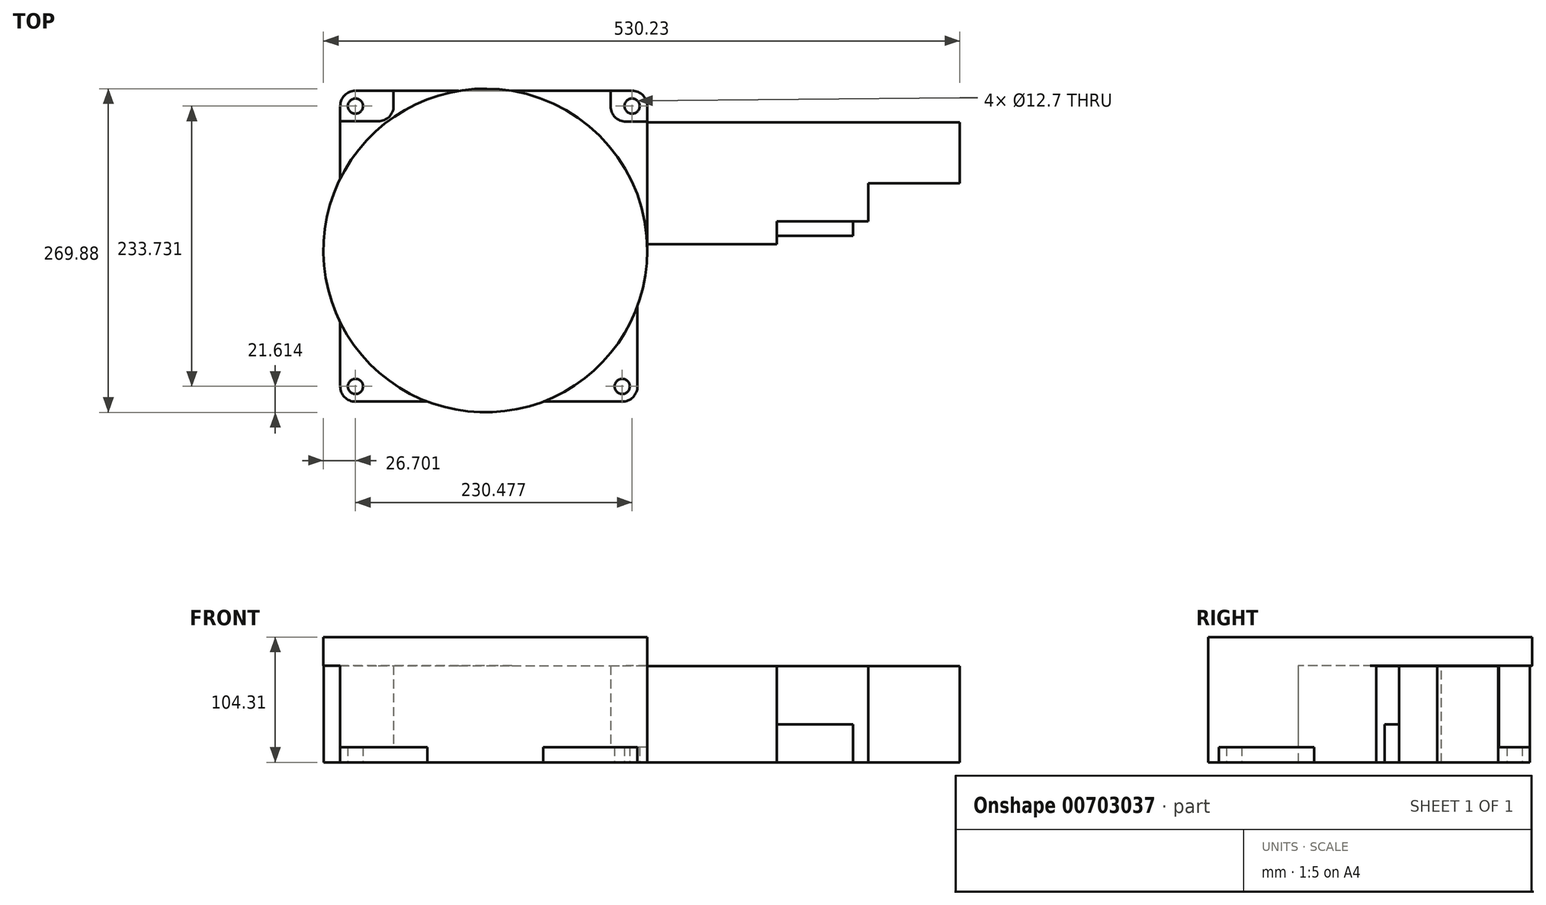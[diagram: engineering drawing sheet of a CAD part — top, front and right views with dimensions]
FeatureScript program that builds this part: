
annotation { "Feature Type Name" : "Feature", "Feature Type Description" : "" }
export const myFeature = defineFeature(function(context is Context, id is Id, definition is map)
    precondition{}
    {
        {
            var Q0;
            Q0=qCreatedBy(makeId("Top.planeOp"),FACE);
            var sketch = newSketch(context, id + "F0", { "sketchPlane" : qUnion([Q0])});
            skLineSegment(sketch, "E0.bottom", {"start": v(-108.24, 133.1) * mm, "end": v(122.24, 133.1) * mm});
            skLineSegment(sketch, "E0.top", {"start": v(-108.24, -126.03) * mm, "end": v(-48.23, -126.03) * mm});
            skLineSegment(sketch, "E0.left", {"start": v(-120.94, 120.4) * mm, "end": v(-120.94, 59.45) * mm});
            skLineSegment(sketch, "E0.right", {"start": v(134.94, 120.4) * mm, "end": v(134.94, 0) * mm});
            skLineSegment(sketch, "E1", {"start": v(126.71, -46.38) * mm, "end": v(126.71, -46.4) * mm});
            skArc(sketch, "E2.filletArc", {"start": v(114.01, -126.03) * mm, "mid": v(123, -122.3) * mm, "end": v(126.71, -113.33) * mm});
            skPoint(sketch, "E3.visualSharp", {"position": v(134.94, 133.1) * mm});
            skArc(sketch, "E3.filletArc", {"start": v(134.94, 120.4) * mm, "mid": v(131.22, 129.39) * mm, "end": v(122.24, 133.1) * mm});
            skPoint(sketch, "E4.visualSharp", {"position": v(-120.94, 133.1) * mm});
            skArc(sketch, "E4.filletArc", {"start": v(-108.24, 133.1) * mm, "mid": v(-117.22, 129.39) * mm, "end": v(-120.94, 120.4) * mm});
            skPoint(sketch, "E5.visualSharp", {"position": v(-120.94, -126.03) * mm});
            skArc(sketch, "E5.filletArc", {"start": v(-120.94, -113.33) * mm, "mid": v(-117.22, -122.3) * mm, "end": v(-108.24, -126.03) * mm});
            skArc(sketch, "E6", {"start": v(-48.23, -126.03) * mm, "mid": v(0, -134.94) * mm, "end": v(48.23, -126.03) * mm});
            skLineSegment(sketch, "E7", {"start": v(126.71, -46.38) * mm, "end": v(126.71, -113.33) * mm});
            skArc(sketch, "E8", {"start": v(126.71, -46.4) * mm, "mid": v(132.86, -23.56) * mm, "end": v(134.94, 0) * mm});
            skLineSegment(sketch, "E9", {"start": v(48.23, -126.03) * mm, "end": v(114.01, -126.03) * mm});
            skArc(sketch, "E10", {"start": v(-120.94, 59.45) * mm, "mid": v(-134.76, 0) * mm, "end": v(-120.94, -59.45) * mm});
            skLineSegment(sketch, "E11", {"start": v(-120.94, -59.45) * mm, "end": v(-120.94, -113.33) * mm});
            skSolve(sketch);
        }
        {
            var Q0;
            Q0 = qSketchRegion(id + "F0", true);
            extrude(context, id + "F1", {"entities" : qUnion([Q0]), "oppositeDirection" : true, "depth" : 12.7 * mm, "offsetDistance" : 25.4 * mm});
        }
        {
            var Q0;
            Q0=makeQuery(id+"F1.opExtrude","CAP_FACE",FACE,{"disambiguationData":[OSD([sQuery(id+"F0.wireOp",EDGE,"E0.bottom"),sQuery(id+"F0.wireOp",EDGE,"E0.top"),sQuery(id+"F0.wireOp",EDGE,"E0.left"),sQuery(id+"F0.wireOp",EDGE,"E0.right"),sQuery(id+"F0.wireOp",EDGE,"E2.filletArc"),sQuery(id+"F0.wireOp",EDGE,"E3.filletArc"),sQuery(id+"F0.wireOp",EDGE,"E4.filletArc"),sQuery(id+"F0.wireOp",EDGE,"E5.filletArc"),sQuery(id+"F0.wireOp",EDGE,"E6"),sQuery(id+"F0.wireOp",EDGE,"E7"),sQuery(id+"F0.wireOp",EDGE,"E8"),sQuery(id+"F0.wireOp",EDGE,"E9")])],"isStart":false});
            var sketch = newSketch(context, id + "F2", { "sketchPlane" : qUnion([Q0])});
            skCircle(sketch, "E12", {"center": v(-108.24, -120.4) * mm, "radius": 6.35 * mm});
            skCircle(sketch, "E13", {"center": v(122.24, -120.4) * mm, "radius": 6.35 * mm});
            skCircle(sketch, "E14", {"center": v(-108.24, 113.33) * mm, "radius": 6.35 * mm});
            skCircle(sketch, "E15", {"center": v(114.01, 113.33) * mm, "radius": 6.35 * mm});
            skSolve(sketch);
        }
        {
            var Q0;
            Q0 = qSketchRegion(id + "F2", true);
            var Q1;
            Q1=makeQuery(id+"F1.opExtrude","CAP_FACE",FACE,{"disambiguationData":[OSD([sQuery(id+"F0.wireOp",EDGE,"E0.bottom"),sQuery(id+"F0.wireOp",EDGE,"E0.top"),sQuery(id+"F0.wireOp",EDGE,"E0.left"),sQuery(id+"F0.wireOp",EDGE,"E0.right"),sQuery(id+"F0.wireOp",EDGE,"E2.filletArc"),sQuery(id+"F0.wireOp",EDGE,"E3.filletArc"),sQuery(id+"F0.wireOp",EDGE,"E4.filletArc"),sQuery(id+"F0.wireOp",EDGE,"E5.filletArc"),sQuery(id+"F0.wireOp",EDGE,"E6"),sQuery(id+"F0.wireOp",EDGE,"E7"),sQuery(id+"F0.wireOp",EDGE,"E8"),sQuery(id+"F0.wireOp",EDGE,"E9")])],"isStart":true});
            var Q2;
            Q2=sQuery(id+"F2.wireOp",EDGE,"E13");
            var Q3;
            Q3=sQuery(id+"F2.wireOp",EDGE,"E12");
            var Q4;
            Q4=sQuery(id+"F2.wireOp",EDGE,"E14");
            var Q5;
            Q5=sQuery(id+"F2.wireOp",EDGE,"E15");
            extrude(context, id + "F3", {"entities" : qUnion([Q0, Q1]), "operationType" : NewBodyOperationType.REMOVE, "surfaceEntities" : qUnion([Q2, Q3, Q4, Q5]), "endBound" : BoundingType.THROUGH_ALL, "oppositeDirection" : true, "depth" : -12.7 * mm, "offsetDistance" : 25.4 * mm});
        }
        {
            var Q0;
            Q0=makeQuery(id+"F1.opExtrude","CAP_FACE",FACE,{"disambiguationData":[OSD([sQuery(id+"F0.wireOp",EDGE,"E0.bottom"),sQuery(id+"F0.wireOp",EDGE,"E0.top"),sQuery(id+"F0.wireOp",EDGE,"E0.left"),sQuery(id+"F0.wireOp",EDGE,"E0.right"),sQuery(id+"F0.wireOp",EDGE,"E2.filletArc"),sQuery(id+"F0.wireOp",EDGE,"E3.filletArc"),sQuery(id+"F0.wireOp",EDGE,"E4.filletArc"),sQuery(id+"F0.wireOp",EDGE,"E5.filletArc"),sQuery(id+"F0.wireOp",EDGE,"E6"),sQuery(id+"F0.wireOp",EDGE,"E7"),sQuery(id+"F0.wireOp",EDGE,"E8"),sQuery(id+"F0.wireOp",EDGE,"E9")])],"isStart":true});
            var sketch = newSketch(context, id + "F4", { "sketchPlane" : qUnion([Q0])});
            skLineSegment(sketch, "E16", {"start": v(-76.49, 133.1) * mm, "end": v(-76.49, 120.4) * mm});
            skLineSegment(sketch, "E17", {"start": v(-120.94, 107.7) * mm, "end": v(-89.19, 107.7) * mm});
            skLineSegment(sketch, "E18", {"start": v(104.3, 133.1) * mm, "end": v(104.3, 120.11) * mm});
            skLineSegment(sketch, "E19", {"start": v(134.94, 107.41) * mm, "end": v(117, 107.41) * mm});
            skArc(sketch, "E20.filletArc", {"start": v(-89.19, 107.7) * mm, "mid": v(-80.2, 111.43) * mm, "end": v(-76.49, 120.4) * mm});
            skArc(sketch, "E21.filletArc", {"start": v(104.3, 120.11) * mm, "mid": v(108.02, 111.13) * mm, "end": v(117, 107.41) * mm});
            skLineSegment(sketch, "E22", {"start": v(98.35, -126.03) * mm, "end": v(98.35, -102.17) * mm});
            skLineSegment(sketch, "E23", {"start": v(98.35, -102.17) * mm, "end": v(126.71, -102.17) * mm});
            skArc(sketch, "E24", {"start": v(-120.3, 61.13) * mm, "mid": v(-31.43, -131.23) * mm, "end": v(134.94, 0) * mm});
            skLineSegment(sketch, "E25", {"start": v(134.94, 107.41) * mm, "end": v(134.94, 0) * mm});
            skSolve(sketch);
        }
        {
            var Q0;
            {var subQ5=sQuery(id+"F4.wireOp",EDGE,"E16");Q0=makeQuery(id+"F4.imprint","IMPRINT",FACE,{"disambiguationData":[TD([[makeQuery(id+"F4.imprint","IMPRINT",EDGE,{"derivedFrom":subQ5}),1.0]])]});}
            extrude(context, id + "F5", {"entities" : qUnion([Q0]), "operationType" : NewBodyOperationType.ADD, "depth" : 67.8 * mm, "offsetDistance" : 25.4 * mm});
        }
        {
            var Q0;
            Q0=makeQuery(id+"F5.opExtrude","CAP_FACE",FACE,{"disambiguationData":[OSD([sQuery(id+"F0.wireOp",EDGE,"E0.bottom"),sQuery(id+"F0.wireOp",EDGE,"E0.left"),sQuery(id+"F0.wireOp",EDGE,"E10"),sQuery(id+"F0.wireOp",EDGE,"E11"),sQuery(id+"F4.wireOp",EDGE,"E16"),sQuery(id+"F4.wireOp",EDGE,"E17"),sQuery(id+"F4.wireOp",EDGE,"E18"),sQuery(id+"F4.wireOp",EDGE,"E19"),sQuery(id+"F4.wireOp",EDGE,"E20.filletArc"),sQuery(id+"F4.wireOp",EDGE,"E21.filletArc"),sQuery(id+"F4.wireOp",EDGE,"E24"),sQuery(id+"F4.wireOp",EDGE,"E25")])],"isStart":false});
            var sketch = newSketch(context, id + "F6", { "sketchPlane" : qUnion([Q0])});
            skCircle(sketch, "E26", {"center": v(0, 0) * mm, "radius": 134.94 * mm});
            skSolve(sketch);
        }
        {
            var Q0;
            Q0 = qSketchRegion(id + "F6", true);
            var Q1;
            Q1 = qSketchRegion(id + "F8", true);
            extrude(context, id + "F7", {"entities" : qUnion([Q0, Q1]), "operationType" : NewBodyOperationType.ADD, "depth" : 23.8 * mm, "offsetDistance" : 25.4 * mm});
        }
        {
            var Q0;
            Q0=makeQuery(id+"F7.opExtrude","CAP_FACE",FACE,{"disambiguationData":[OSD([sQuery(id+"F6.wireOp",EDGE,"E26")])],"isStart":false});
            var sketch = newSketch(context, id + "F8", { "sketchPlane" : qUnion([Q0])});
            skCircle(sketch, "E27", {"center": v(-57.15, 57.15) * mm, "radius": 5 * mm});
            skCircle(sketch, "E28", {"center": v(57.15, 57.15) * mm, "radius": 5 * mm});
            skCircle(sketch, "E29", {"center": v(57.15, -57.15) * mm, "radius": 5 * mm});
            skCircle(sketch, "E30", {"center": v(-57.15, -57.15) * mm, "radius": 5 * mm});
            skSolve(sketch);
        }
        {
            var Q0;
            Q0=makeQuery(id+"F5.boolean.opBoolean","MERGE",FACE,{"derivedFrom":[makeQuery(id+"F1.opExtrude","SWEPT_FACE",FACE,{"disambiguationData":[OSD([sQuery(id+"F0.wireOp",EDGE,"E0.right")])]}),makeQuery(id+"F5.opExtrude","SWEPT_FACE",FACE,{"disambiguationData":[OSD([sQuery(id+"F4.wireOp",EDGE,"E25")])]})]});
            var sketch = newSketch(context, id + "F9", { "sketchPlane" : qUnion([Q0])});
            skLineSegment(sketch, "E31.bottom", {"start": v(5.35, 67.38) * mm, "end": v(106.95, 67.38) * mm});
            skLineSegment(sketch, "E31.top", {"start": v(5.35, -12.7) * mm, "end": v(106.95, -12.7) * mm});
            skLineSegment(sketch, "E31.left", {"start": v(5.35, 67.38) * mm, "end": v(5.35, -12.7) * mm});
            skLineSegment(sketch, "E31.right", {"start": v(106.95, 67.38) * mm, "end": v(106.95, -12.7) * mm});
            skSolve(sketch);
        }
        {
            var Q0;
            Q0 = qSketchRegion(id + "F9", true);
            extrude(context, id + "F10", {"entities" : qUnion([Q0]), "operationType" : NewBodyOperationType.ADD, "depth" : 107.95 * mm, "offsetDistance" : 25.4 * mm});
        }
        {
            var Q0;
            Q0=makeQuery(id+"F10.opExtrude","CAP_FACE",FACE,{"disambiguationData":[OSD([sQuery(id+"F9.wireOp",EDGE,"E31.bottom"),sQuery(id+"F9.wireOp",EDGE,"E31.top"),sQuery(id+"F9.wireOp",EDGE,"E31.left"),sQuery(id+"F9.wireOp",EDGE,"E31.right")])],"isStart":false});
            var sketch = newSketch(context, id + "F11", { "sketchPlane" : qUnion([Q0])});
            skLineSegment(sketch, "E32.bottom", {"start": v(24.4, 67.38) * mm, "end": v(106.95, 67.38) * mm});
            skLineSegment(sketch, "E32.top", {"start": v(24.4, -12.7) * mm, "end": v(106.95, -12.7) * mm});
            skLineSegment(sketch, "E32.left", {"start": v(24.4, 67.38) * mm, "end": v(24.4, -12.7) * mm});
            skLineSegment(sketch, "E32.right", {"start": v(106.95, 67.38) * mm, "end": v(106.95, -12.7) * mm});
            skSolve(sketch);
        }
        {
            var Q0;
            Q0 = qSketchRegion(id + "F11", true);
            extrude(context, id + "F12", {"entities" : qUnion([Q0]), "operationType" : NewBodyOperationType.ADD, "depth" : 76.2 * mm, "offsetDistance" : 25.4 * mm});
        }
        {
            var Q0;
            Q0=makeQuery(id+"F10.opExtrude","CAP_FACE",FACE,{"disambiguationData":[OSD([sQuery(id+"F9.wireOp",EDGE,"E31.bottom"),sQuery(id+"F9.wireOp",EDGE,"E31.top"),sQuery(id+"F9.wireOp",EDGE,"E31.left"),sQuery(id+"F9.wireOp",EDGE,"E31.right")])],"isStart":false});
            var sketch = newSketch(context, id + "F13", { "sketchPlane" : qUnion([Q0])});
            skLineSegment(sketch, "E33.bottom", {"start": v(12.1, 19.05) * mm, "end": v(24.4, 19.05) * mm});
            skLineSegment(sketch, "E33.top", {"start": v(12.1, -12.7) * mm, "end": v(24.4, -12.7) * mm});
            skLineSegment(sketch, "E33.left", {"start": v(12.1, 19.05) * mm, "end": v(12.1, -12.7) * mm});
            skLineSegment(sketch, "E33.right", {"start": v(24.4, 19.05) * mm, "end": v(24.4, -12.7) * mm});
            skSolve(sketch);
        }
        {
            var Q0;
            Q0=makeQuery(id+"F13.imprint","IMPRINT",FACE,{"disambiguationData":[TD([[makeQuery(id+"F13.imprint","IMPRINT",EDGE,{"derivedFrom":sQuery(id+"F13.wireOp",EDGE,"E33.bottom")}),-1.0]])]});
            extrude(context, id + "F14", {"entities" : qUnion([Q0]), "operationType" : NewBodyOperationType.ADD, "depth" : 63.5 * mm, "offsetDistance" : 25.4 * mm});
        }
        {
            var Q0;
            Q0=makeQuery(id+"F12.opExtrude","CAP_FACE",FACE,{"disambiguationData":[OSD([sQuery(id+"F11.wireOp",EDGE,"E32.bottom"),sQuery(id+"F11.wireOp",EDGE,"E32.top"),sQuery(id+"F11.wireOp",EDGE,"E32.left"),sQuery(id+"F11.wireOp",EDGE,"E32.right")])],"isStart":false});
            var sketch = newSketch(context, id + "F15", { "sketchPlane" : qUnion([Q0])});
            skLineSegment(sketch, "E34.bottom", {"start": v(56.15, 67.38) * mm, "end": v(106.95, 67.38) * mm});
            skLineSegment(sketch, "E34.top", {"start": v(56.15, -12.7) * mm, "end": v(106.95, -12.7) * mm});
            skLineSegment(sketch, "E34.left", {"start": v(56.15, 67.38) * mm, "end": v(56.15, -12.7) * mm});
            skLineSegment(sketch, "E34.right", {"start": v(106.95, 67.38) * mm, "end": v(106.95, -12.7) * mm});
            skSolve(sketch);
        }
        {
            var Q0;
            Q0 = qSketchRegion(id + "F15", true);
            extrude(context, id + "F16", {"entities" : qUnion([Q0]), "operationType" : NewBodyOperationType.ADD, "depth" : 76.2 * mm, "offsetDistance" : 25.4 * mm});
        }
    });
